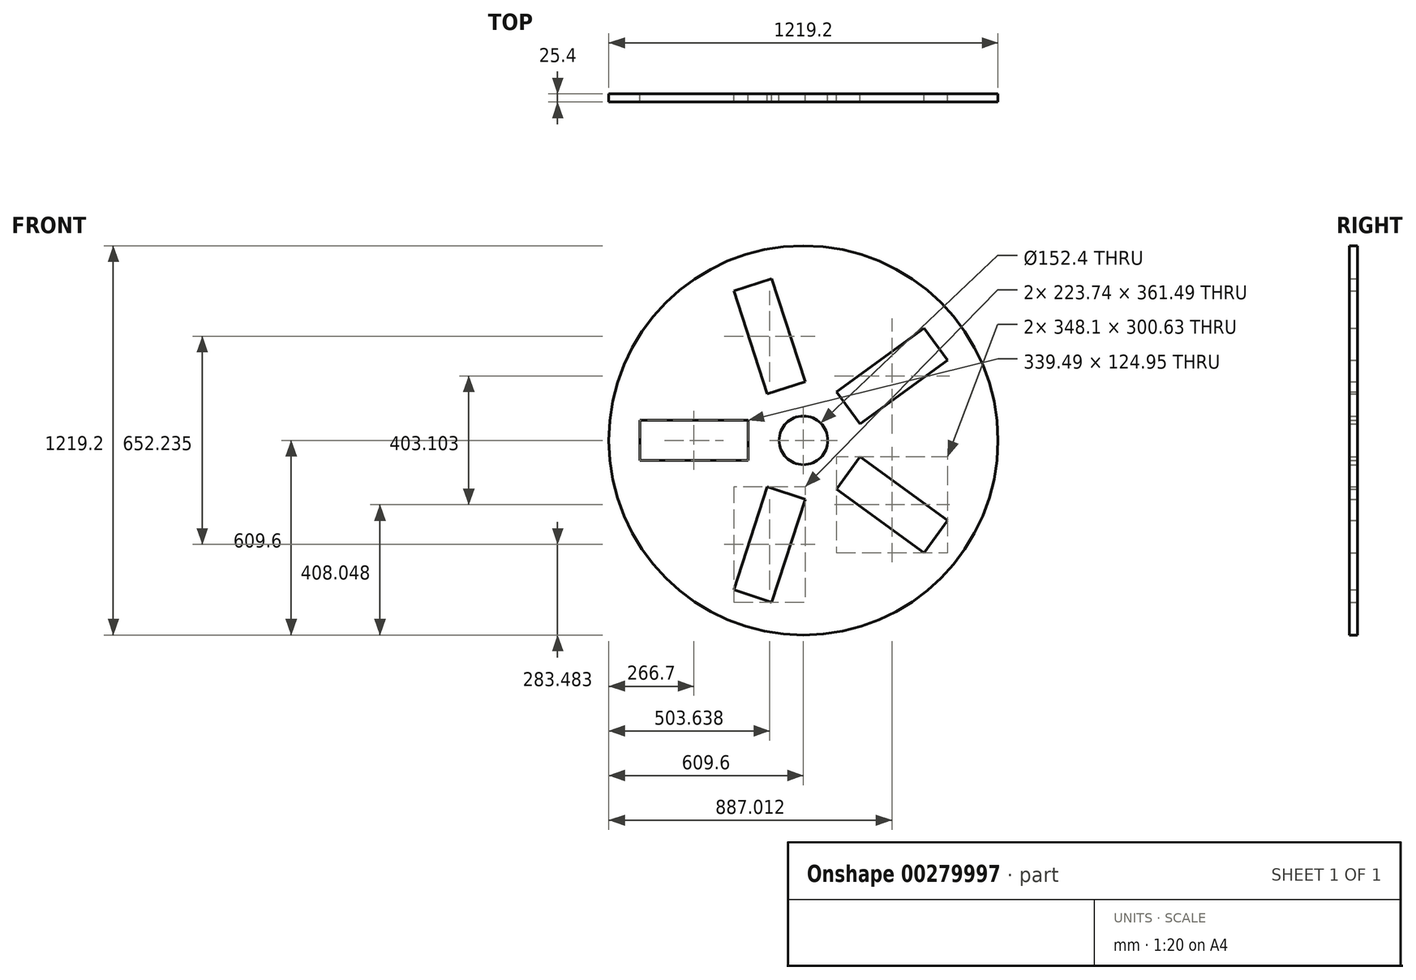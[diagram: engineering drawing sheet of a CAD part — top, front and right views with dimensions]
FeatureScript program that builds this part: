
annotation { "Feature Type Name" : "Feature", "Feature Type Description" : "" }
export const myFeature = defineFeature(function(context is Context, id is Id, definition is map)
    precondition{}
    {
        {
            var Q0;
            Q0=qCreatedBy(makeId("Front.planeOp"),FACE);
            var sketch = newSketch(context, id + "F0", { "sketchPlane" : qUnion([Q0])});
            skCircle(sketch, "E0", {"center": v(0, 0) * mm, "radius": 609.6 * mm});
            skCircle(sketch, "E1", {"center": v(0, 0) * mm, "radius": 76.2 * mm});
            skLineSegment(sketch, "E2.bottom", {"start": v(-173.16, 62.48) * mm, "end": v(-512.64, 62.48) * mm});
            skLineSegment(sketch, "E2.top", {"start": v(-173.16, -62.48) * mm, "end": v(-512.64, -62.48) * mm});
            skLineSegment(sketch, "E2.left", {"start": v(-173.16, 62.48) * mm, "end": v(-173.16, -62.48) * mm});
            skLineSegment(sketch, "E2.right", {"start": v(-512.64, 62.48) * mm, "end": v(-512.64, -62.48) * mm});
            skPoint(sketch, "E2.middle", {"position": v(-342.9, 0) * mm});
            skLineSegment(sketch, "E3", {"start": v(-76.2, 0) * mm, "end": v(-609.6, 0) * mm});
            skLineSegment(sketch, "E4.1.0", {"start": v(-217.83, -468.25) * mm, "end": v(-99, -506.86) * mm});
            skLineSegment(sketch, "E4.1.1", {"start": v(-112.93, -145.37) * mm, "end": v(-217.83, -468.25) * mm});
            skLineSegment(sketch, "E4.1.2", {"start": v(-112.93, -145.37) * mm, "end": v(5.9, -183.99) * mm});
            skLineSegment(sketch, "E4.1.3", {"start": v(5.9, -183.99) * mm, "end": v(-99, -506.86) * mm});
            skLineSegment(sketch, "E4.2.0", {"start": v(378.02, -351.87) * mm, "end": v(451.46, -250.78) * mm});
            skLineSegment(sketch, "E4.2.1", {"start": v(103.36, -152.32) * mm, "end": v(378.02, -351.87) * mm});
            skLineSegment(sketch, "E4.2.2", {"start": v(103.36, -152.32) * mm, "end": v(176.8, -51.23) * mm});
            skLineSegment(sketch, "E4.2.3", {"start": v(176.8, -51.23) * mm, "end": v(451.46, -250.78) * mm});
            skLineSegment(sketch, "E5.2.3.0", {"start": v(451.46, 250.78) * mm, "end": v(378.02, 351.87) * mm});
            skLineSegment(sketch, "E5.3.3.0", {"start": v(176.8, 51.23) * mm, "end": v(451.46, 250.78) * mm});
            skLineSegment(sketch, "E5.6.3.0", {"start": v(176.8, 51.23) * mm, "end": v(103.36, 152.32) * mm});
            skLineSegment(sketch, "E5.9.3.0", {"start": v(103.36, 152.32) * mm, "end": v(378.02, 351.87) * mm});
            skLineSegment(sketch, "E5.2.4.0", {"start": v(-99, 506.86) * mm, "end": v(-217.83, 468.25) * mm});
            skLineSegment(sketch, "E5.3.4.0", {"start": v(5.9, 183.99) * mm, "end": v(-99, 506.86) * mm});
            skLineSegment(sketch, "E5.6.4.0", {"start": v(5.9, 183.99) * mm, "end": v(-112.93, 145.37) * mm});
            skLineSegment(sketch, "E5.9.4.0", {"start": v(-112.93, 145.37) * mm, "end": v(-217.83, 468.25) * mm});
            skSolve(sketch);
        }
        {
            var Q0;
            Q0=qSketchRegion(id+"F0",true);
            var Q1;
            Q1=makeQuery(id+"F0.imprint","IMPRINT",FACE,{"disambiguationData":[TD([[makeQuery(id+"F0.imprint","IMPRINT",EDGE,{"derivedFrom":sQuery(id+"F0.wireOp",EDGE,"E0")}),1.0]])]});
            extrude(context, id + "F1", {"entities" : qUnion([Q0, Q1]), "depth" : 25.4 * mm});
        }
    });
